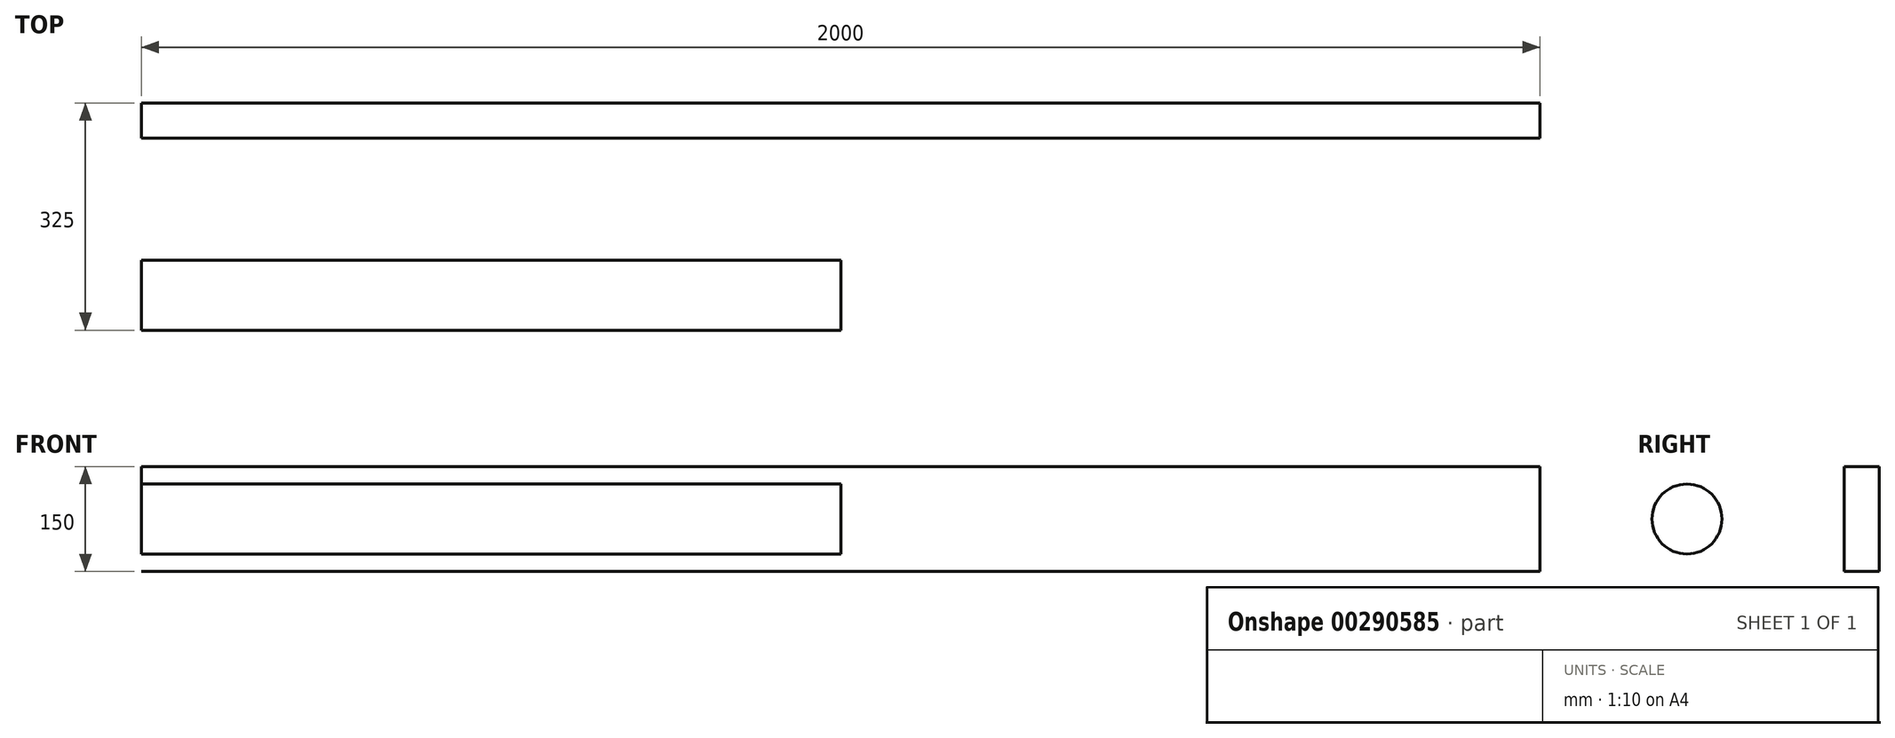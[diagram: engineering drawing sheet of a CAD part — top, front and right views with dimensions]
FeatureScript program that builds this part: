
annotation { "Feature Type Name" : "Feature", "Feature Type Description" : "" }
export const myFeature = defineFeature(function(context is Context, id is Id, definition is map)
    precondition{}
    {
        {
            var Q0;
            Q0=qCreatedBy(makeId("Right.planeOp"),FACE);
            var sketch = newSketch(context, id + "F0", { "sketchPlane" : qUnion([Q0])});
            skLineSegment(sketch, "E0.bottom", {"start": v(-25, 75) * mm, "end": v(25, 75) * mm});
            skLineSegment(sketch, "E0.top", {"start": v(-25, -75) * mm, "end": v(25, -75) * mm});
            skLineSegment(sketch, "E0.left", {"start": v(-25, 75) * mm, "end": v(-25, -75) * mm});
            skLineSegment(sketch, "E0.right", {"start": v(25, 75) * mm, "end": v(25, -75) * mm});
            skSolve(sketch);
        }
        {
            var Q0;
            Q0=makeQuery(id+"F0.imprint","IMPRINT",FACE,{"disambiguationData":[TD([[makeQuery(id+"F0.imprint","IMPRINT",EDGE,{"derivedFrom":sQuery(id+"F0.wireOp",EDGE,"E0.bottom")}),-1.0]])]});
            extrude(context, id + "F1", {"entities" : qUnion([Q0]), "depth" : 2000 * mm});
        }
        {
            var Q0;
            Q0=qCreatedBy(makeId("Right.planeOp"),FACE);
            var sketch = newSketch(context, id + "F2", { "sketchPlane" : qUnion([Q0])});
            skCircle(sketch, "E1", {"center": v(-250, 0) * mm, "radius": 50 * mm});
            skSolve(sketch);
        }
        {
            var Q0;
            Q0 = qSketchRegion(id + "F2", true);
            extrude(context, id + "F3", {"entities" : qUnion([Q0]), "depth" : 1000 * mm});
        }
    });
